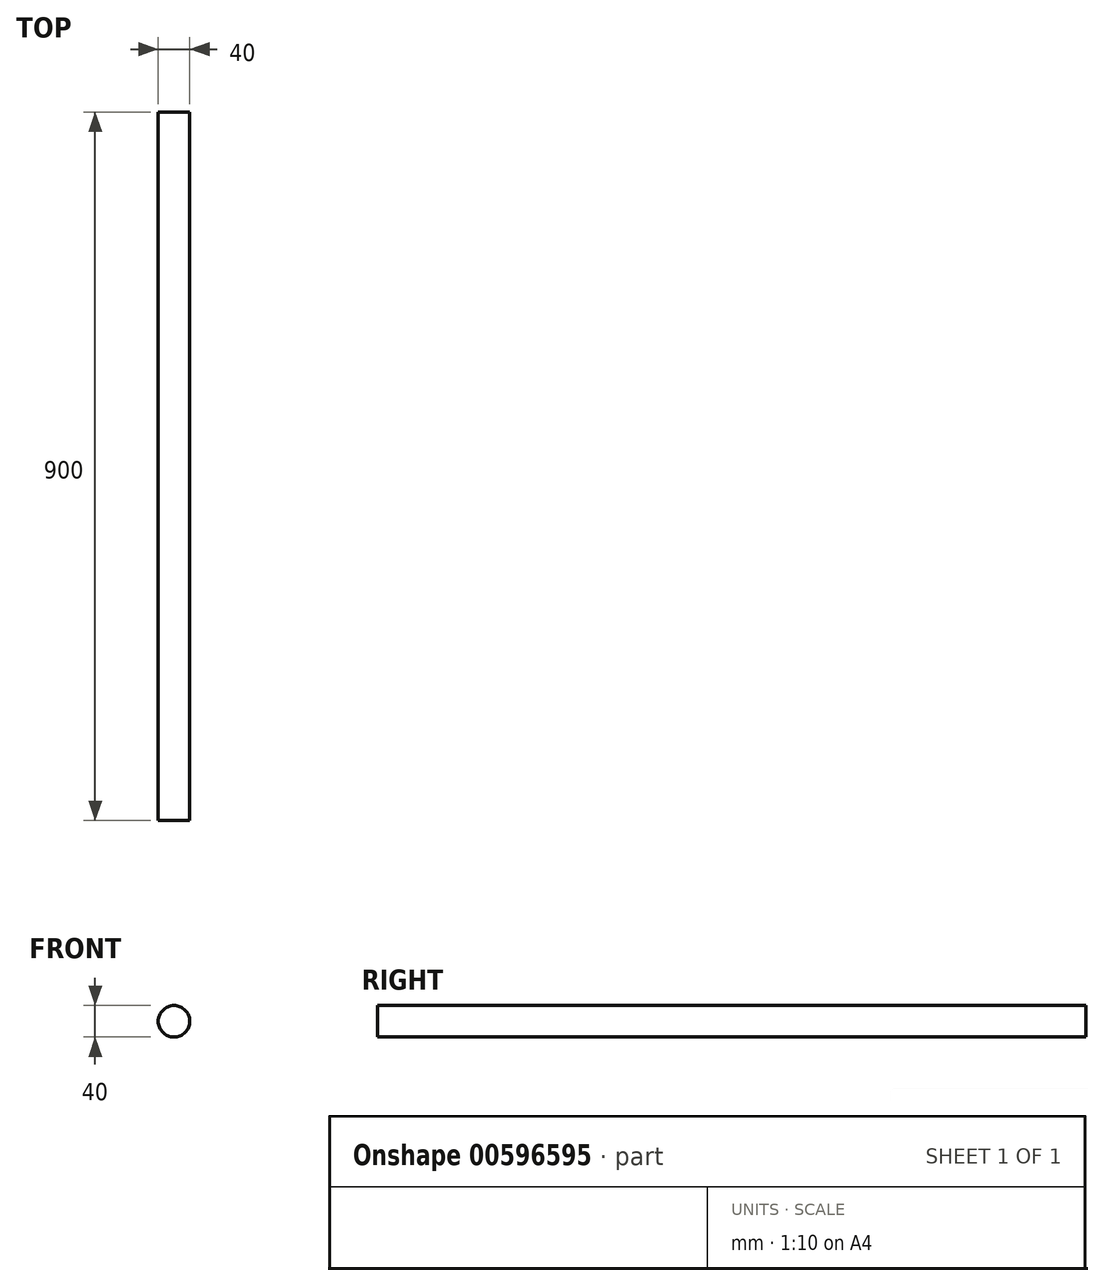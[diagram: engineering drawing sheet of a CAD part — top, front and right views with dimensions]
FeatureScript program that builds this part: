
annotation { "Feature Type Name" : "Feature", "Feature Type Description" : "" }
export const myFeature = defineFeature(function(context is Context, id is Id, definition is map)
    precondition{}
    {
        {
            var Q0;
            Q0=qCreatedBy(makeId("Front.planeOp"),FACE);
            var sketch = newSketch(context, id + "F0", { "sketchPlane" : qUnion([Q0])});
            skCircle(sketch, "E0", {"center": v(0, 0) * mm, "radius": 20 * mm});
            skSolve(sketch);
        }
        {
            var Q0;
            Q0=makeQuery(id+"F0.imprint","IMPRINT",FACE,{"disambiguationData":[TD([[makeQuery(id+"F0.imprint","IMPRINT",EDGE,{"derivedFrom":sQuery(id+"F0.wireOp",EDGE,"E0")}),1.0]])]});
            extrude(context, id + "F1", {"entities" : qUnion([Q0]), "depth" : 900 * mm, "offsetDistance" : 25 * mm});
        }
    });
